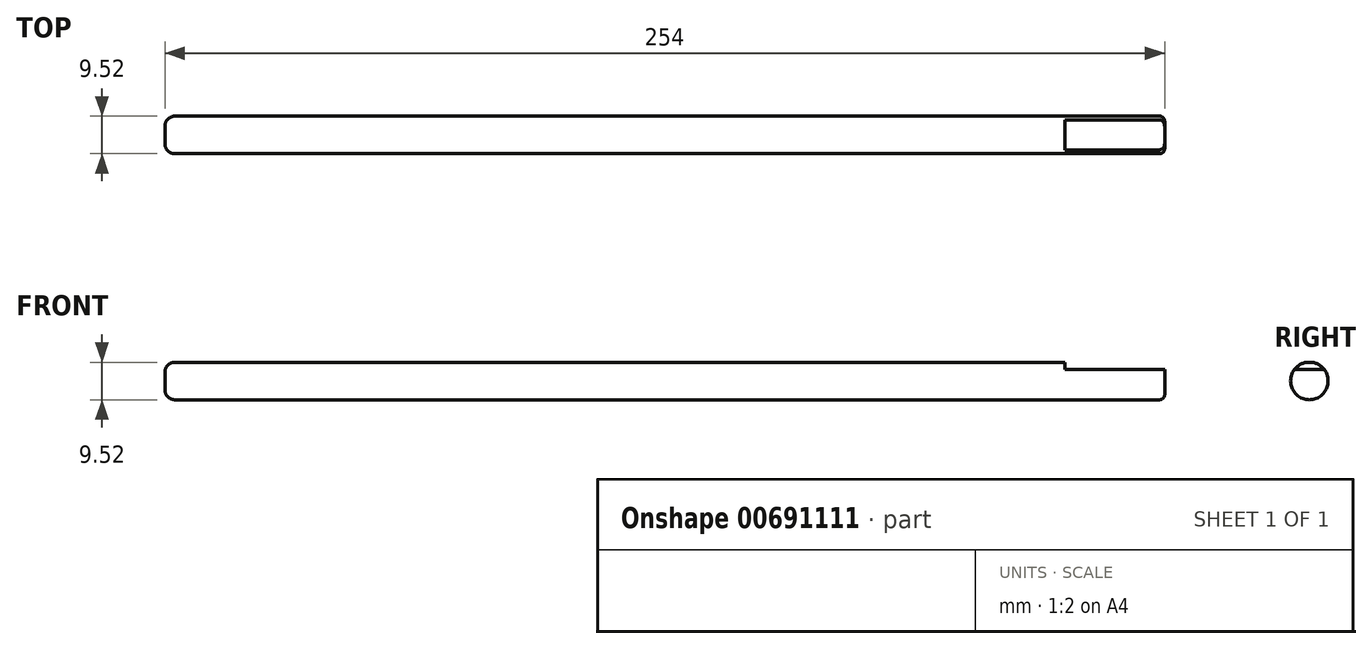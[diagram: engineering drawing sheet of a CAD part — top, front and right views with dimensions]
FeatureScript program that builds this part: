
annotation { "Feature Type Name" : "Feature", "Feature Type Description" : "" }
export const myFeature = defineFeature(function(context is Context, id is Id, definition is map)
    precondition{}
    {
        {
            var Q0;
            Q0=qCreatedBy(makeId("Front.planeOp"),FACE);
            var sketch = newSketch(context, id + "F0", { "sketchPlane" : qUnion([Q0])});
            skLineSegment(sketch, "E0", {"start": v(-101.6, 0) * mm, "end": v(152.4, 0) * mm, "construction": true});
            skLineSegment(sketch, "E1", {"start": v(-101.6, 0) * mm, "end": v(-101.6, 4.76) * mm});
            skLineSegment(sketch, "E2", {"start": v(-101.6, 4.76) * mm, "end": v(152.4, 4.76) * mm});
            skLineSegment(sketch, "E3", {"start": v(152.4, 4.76) * mm, "end": v(152.4, 0) * mm});
            skLineSegment(sketch, "E4", {"start": v(-101.6, 0) * mm, "end": v(152.4, 0) * mm});
            skSolve(sketch);
        }
        {
            var Q0;
            Q0=makeQuery(id+"F0.imprint","IMPRINT",FACE,{"disambiguationData":[TD([[makeQuery(id+"F0.imprint","IMPRINT",EDGE,{"derivedFrom":sQuery(id+"F0.wireOp",EDGE,"E1")}),-1.0]])]});
            var Q1;
            Q1=sQuery(id+"F0.wireOp",EDGE,"E4");
            revolve(context, id + "F1", {"entities" : qUnion([Q0]), "axis" : qUnion([Q1]), "revolveType" : RevolveType.FULL});
        }
        {
            var Q0;
            Q0=makeQuery(id+"F1.opRevolve","SWEPT_FACE",FACE,{"disambiguationData":[OSD([sQuery(id+"F0.wireOp",EDGE,"E3")])]});
            var sketch = newSketch(context, id + "F2", { "sketchPlane" : qUnion([Q0])});
            skLineSegment(sketch, "E5", {"start": v(-3.78, 2.9) * mm, "end": v(3.78, 2.9) * mm});
            skArc(sketch, "E6", {"start": v(-3.78, 2.9) * mm, "mid": v(0, 4.76) * mm, "end": v(3.78, 2.9) * mm});
            skSolve(sketch);
        }
        {
            var Q0;
            Q0 = qSketchRegion(id + "F2", true);
            extrude(context, id + "F3", {"entities" : qUnion([Q0]), "operationType" : NewBodyOperationType.REMOVE, "oppositeDirection" : true, "depth" : 25.4 * mm, "offsetDistance" : 25.4 * mm});
        }
        {
            var Q0;
            Q0=makeQuery(id+"F1.opRevolve","SWEPT_EDGE",EDGE,{"disambiguationData":[OSD([sQuery(id+"F0.wireOp",EDGE,"E1"),sQuery(id+"F0.wireOp",EDGE,"E2")])]});
            fillet(context, id + "F4", {"entities" : qUnion([Q0]), "radius" : 2.54 * mm, "tangentPropagation" : true, "allowEdgeOverflow" : false});
        }
        {
            var Q0;
            Q0=makeQuery(id+"F1.opRevolve","SWEPT_EDGE",EDGE,{"disambiguationData":[OSD([sQuery(id+"F0.wireOp",EDGE,"E2"),sQuery(id+"F0.wireOp",EDGE,"E3")])]});
            fillet(context, id + "F5", {"entities" : qUnion([Q0]), "radius" : 1.27 * mm, "tangentPropagation" : true, "allowEdgeOverflow" : false});
        }
    });
